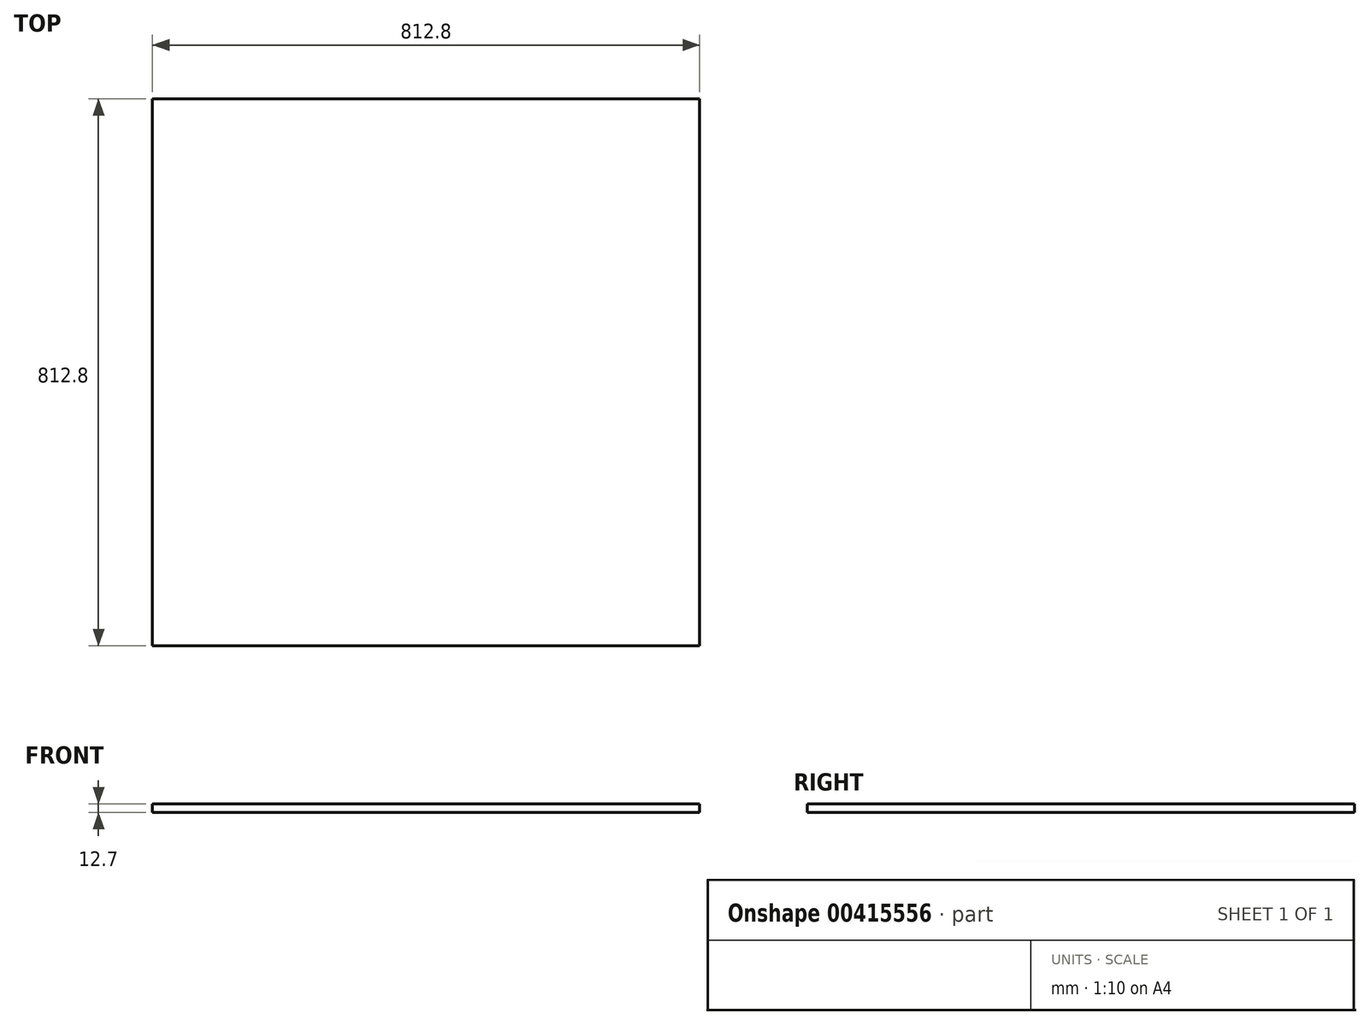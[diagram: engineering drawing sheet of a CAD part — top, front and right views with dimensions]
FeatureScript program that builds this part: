
annotation { "Feature Type Name" : "Feature", "Feature Type Description" : "" }
export const myFeature = defineFeature(function(context is Context, id is Id, definition is map)
    precondition{}
    {
        {
            var Q0;
            Q0=qCreatedBy(makeId("Top.planeOp"),FACE);
            var sketch = newSketch(context, id + "F0", { "sketchPlane" : qUnion([Q0])});
            skLineSegment(sketch, "E0.bottom", {"start": v(406.4, 406.4) * mm, "end": v(-406.4, 406.4) * mm});
            skLineSegment(sketch, "E0.top", {"start": v(406.4, -406.4) * mm, "end": v(-406.4, -406.4) * mm});
            skLineSegment(sketch, "E0.left", {"start": v(406.4, 406.4) * mm, "end": v(406.4, -406.4) * mm});
            skLineSegment(sketch, "E0.right", {"start": v(-406.4, 406.4) * mm, "end": v(-406.4, -406.4) * mm});
            skPoint(sketch, "E0.middle", {"position": v(0, 0) * mm});
            skSolve(sketch);
        }
        {
            var Q0;
            Q0=makeQuery(id+"F0.imprint","IMPRINT",FACE,{"disambiguationData":[TD([[makeQuery(id+"F0.imprint","IMPRINT",EDGE,{"derivedFrom":sQuery(id+"F0.wireOp",EDGE,"E0.bottom")}),1.0]])]});
            extrude(context, id + "F1", {"entities" : qUnion([Q0]), "depth" : 12.7 * mm});
        }
    });
